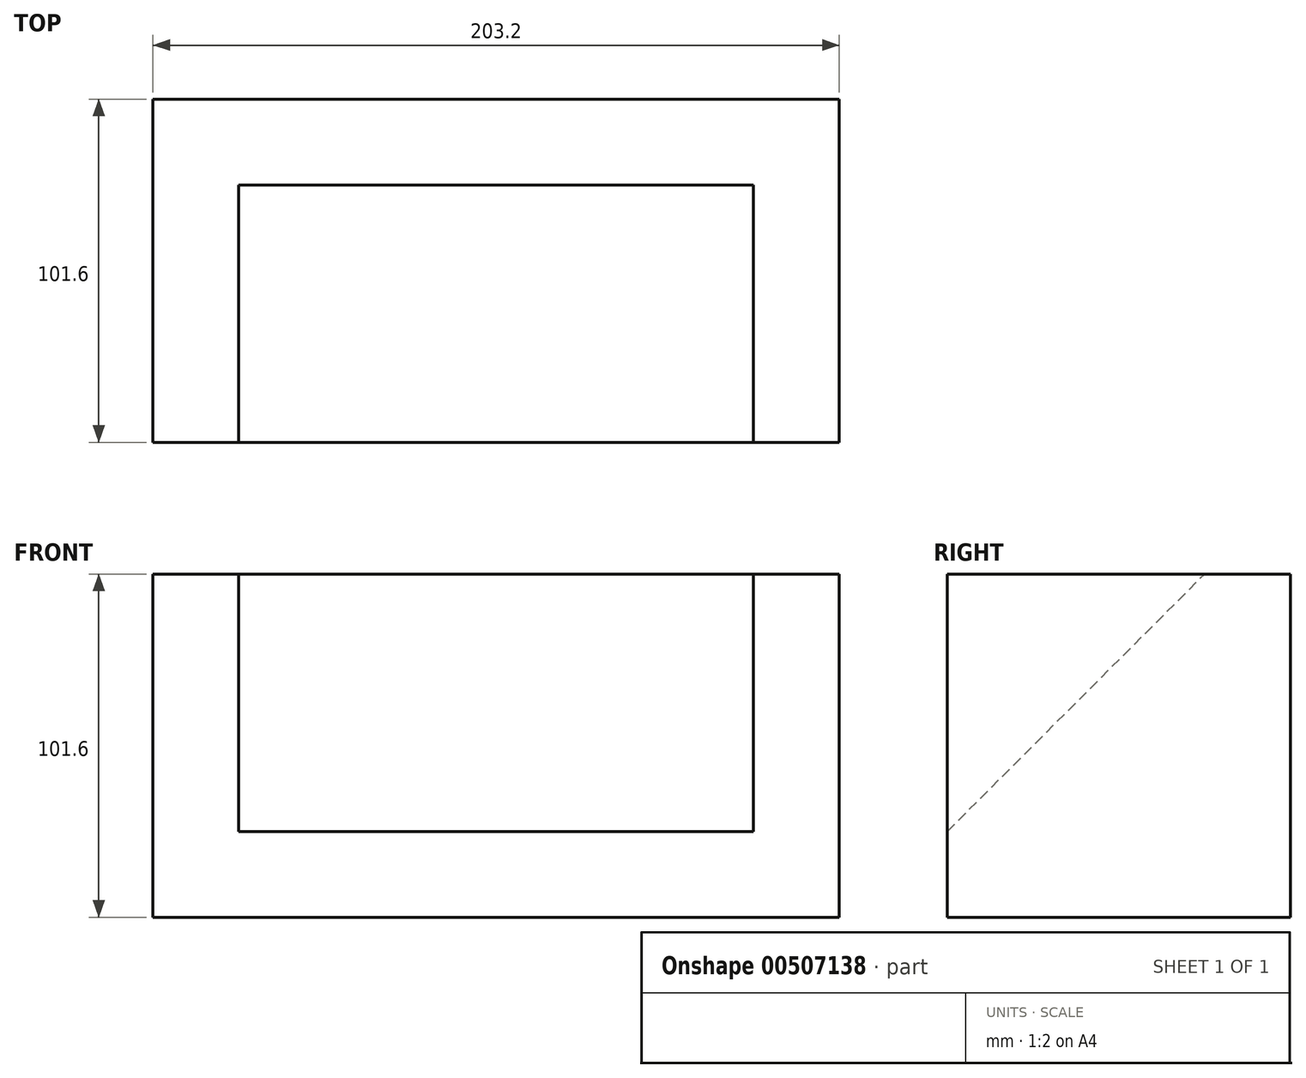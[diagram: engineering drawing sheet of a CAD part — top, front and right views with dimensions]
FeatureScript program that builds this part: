
annotation { "Feature Type Name" : "Feature", "Feature Type Description" : "" }
export const myFeature = defineFeature(function(context is Context, id is Id, definition is map)
    precondition{}
    {
        {
            var Q0;
            Q0=qCreatedBy(makeId("Front.planeOp"),FACE);
            var sketch = newSketch(context, id + "F0", { "sketchPlane" : qUnion([Q0])});
            skLineSegment(sketch, "E0.bottom", {"start": v(101.6, -50.8) * mm, "end": v(-101.6, -50.8) * mm});
            skLineSegment(sketch, "E0.top", {"start": v(101.6, 50.8) * mm, "end": v(-101.6, 50.8) * mm});
            skLineSegment(sketch, "E0.left", {"start": v(101.6, -50.8) * mm, "end": v(101.6, 50.8) * mm});
            skLineSegment(sketch, "E0.right", {"start": v(-101.6, -50.8) * mm, "end": v(-101.6, 50.8) * mm});
            skPoint(sketch, "E0.middle", {"position": v(0, 0) * mm});
            skSolve(sketch);
        }
        {
            var Q0;
            Q0 = qSketchRegion(id + "F0", true);
            extrude(context, id + "F1", {"entities" : qUnion([Q0]), "depth" : 101.6 * mm});
        }
        {
            var Q0;
            Q0=makeQuery(id+"F1.opExtrude","SWEPT_FACE",FACE,{"disambiguationData":[OSD([sQuery(id+"F0.wireOp",EDGE,"E0.right")])]});
            var sketch = newSketch(context, id + "F2", { "sketchPlane" : qUnion([Q0])});
            skLineSegment(sketch, "E1", {"start": v(25.4, 50.8) * mm, "end": v(101.6, 50.8) * mm});
            skLineSegment(sketch, "E2", {"start": v(101.6, 50.8) * mm, "end": v(101.6, -25.4) * mm});
            skLineSegment(sketch, "E3", {"start": v(101.6, -25.4) * mm, "end": v(25.4, 50.8) * mm});
            skSolve(sketch);
        }
        {
            var Q0;
            Q0=makeQuery(id+"F2.imprint","IMPRINT",FACE,{"disambiguationData":[TD([[makeQuery(id+"F2.imprint","IMPRINT",EDGE,{"derivedFrom":sQuery(id+"F2.wireOp",EDGE,"E1")}),1.0]])]});
            extrude(context, id + "F3", {"entities" : qUnion([Q0]), "operationType" : NewBodyOperationType.REMOVE, "oppositeDirection" : true, "depth" : 203.2 * mm});
        }
        {
            var Q0;
            Q0=makeQuery(id+"F2.imprint","IMPRINT",FACE,{"disambiguationData":[TD([[makeQuery(id+"F2.imprint","IMPRINT",EDGE,{"derivedFrom":sQuery(id+"F2.wireOp",EDGE,"E1")}),1.0]])]});
            extrude(context, id + "F4", {"entities" : qUnion([Q0]), "operationType" : NewBodyOperationType.ADD, "oppositeDirection" : true, "depth" : 25.4 * mm});
        }
        {
            var Q0;
            Q0=makeQuery(id+"F1.opExtrude","SWEPT_FACE",FACE,{"disambiguationData":[OSD([sQuery(id+"F0.wireOp",EDGE,"E0.left")])]});
            var sketch = newSketch(context, id + "F5", { "sketchPlane" : qUnion([Q0])});
            skLineSegment(sketch, "E4", {"start": v(-25.4, 50.8) * mm, "end": v(-101.6, 50.8) * mm});
            skLineSegment(sketch, "E5", {"start": v(-101.6, 50.8) * mm, "end": v(-101.6, -25.4) * mm});
            skLineSegment(sketch, "E6", {"start": v(-101.6, -25.4) * mm, "end": v(-25.4, 50.8) * mm});
            skSolve(sketch);
        }
        {
            var Q0;
            Q0=makeQuery(id+"F5.imprint","IMPRINT",FACE,{"disambiguationData":[TD([[makeQuery(id+"F5.imprint","IMPRINT",EDGE,{"derivedFrom":sQuery(id+"F5.wireOp",EDGE,"E4")}),1.0]])]});
            extrude(context, id + "F6", {"entities" : qUnion([Q0]), "operationType" : NewBodyOperationType.ADD, "oppositeDirection" : true, "depth" : 25.4 * mm});
        }
    });
